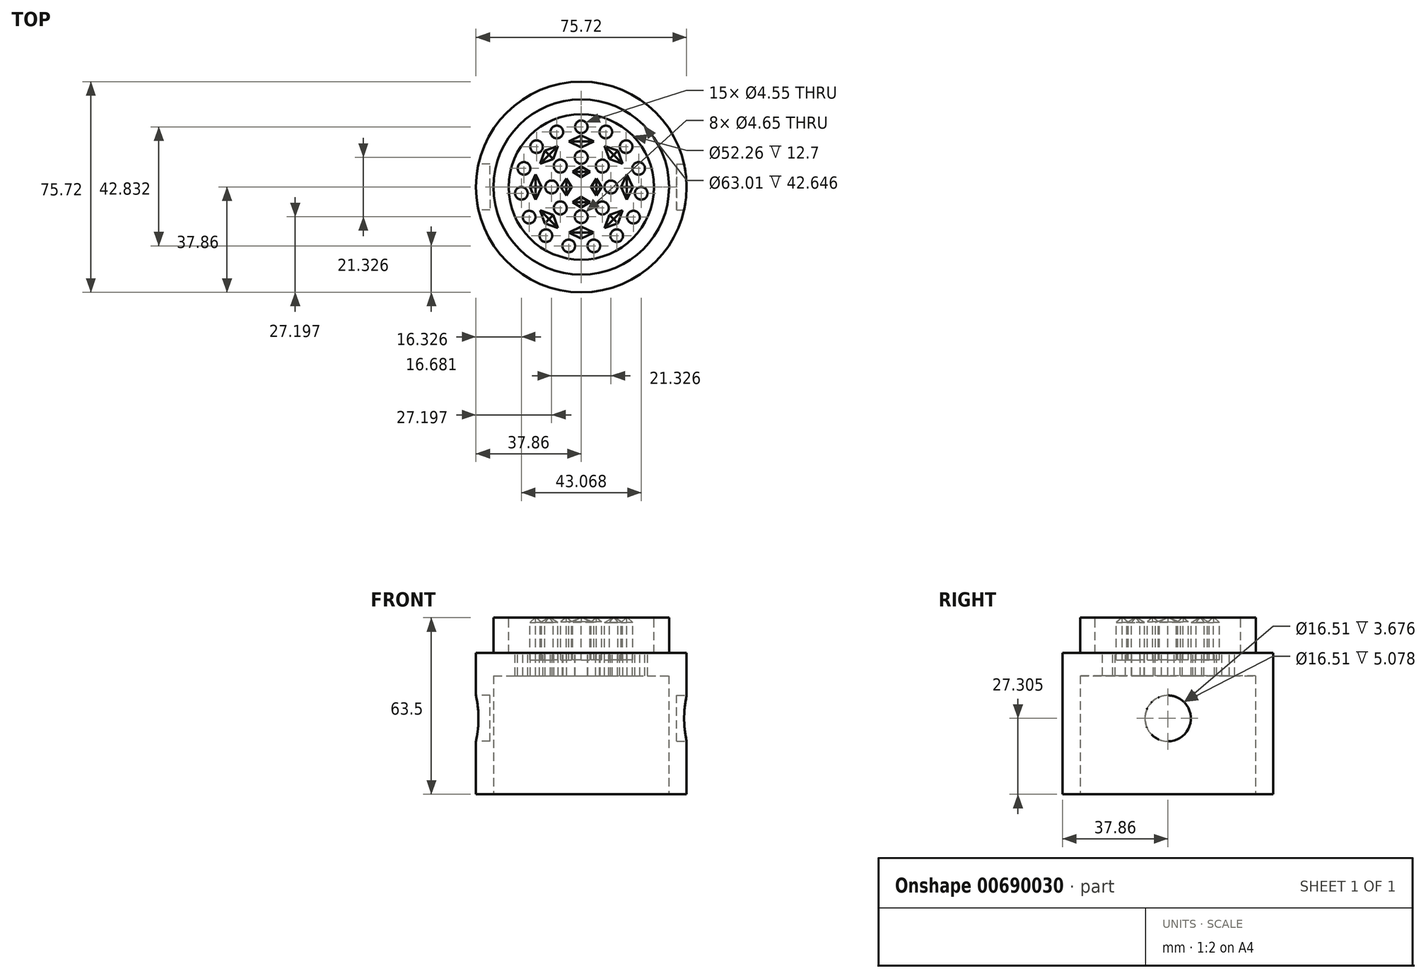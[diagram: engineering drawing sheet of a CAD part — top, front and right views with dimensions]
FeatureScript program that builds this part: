
annotation { "Feature Type Name" : "Feature", "Feature Type Description" : "" }
export const myFeature = defineFeature(function(context is Context, id is Id, definition is map)
    precondition{}
    {
        {
            var Q0;
            Q0=qCreatedBy(makeId("Top.planeOp"),FACE);
            var sketch = newSketch(context, id + "F0", { "sketchPlane" : qUnion([Q0])});
            skCircle(sketch, "E0", {"center": v(0, 0) * mm, "radius": 37.86 * mm});
            skCircle(sketch, "E1", {"center": v(0, 0) * mm, "radius": 31.55 * mm});
            skCircle(sketch, "E2", {"center": v(0, 0) * mm, "radius": 26.13 * mm});
            skCircle(sketch, "E3", {"center": v(0, 0) * mm, "radius": 18.32 * mm});
            skCircle(sketch, "E4", {"center": v(0, 0) * mm, "radius": 14.26 * mm});
            skCircle(sketch, "E5", {"center": v(0, 0) * mm, "radius": 7.5 * mm});
            skCircle(sketch, "E6", {"center": v(0, 0) * mm, "radius": 3.72 * mm});
            skSolve(sketch);
        }
        {
            var Q0;
            Q0=makeQuery(id+"F0.imprint","IMPRINT",FACE,{"disambiguationData":[TD([[makeQuery(id+"F0.imprint","IMPRINT",EDGE,{"derivedFrom":sQuery(id+"F0.wireOp",EDGE,"E0")}),1.0]])]});
            var Q1;
            Q1=makeQuery(id+"F0.imprint","IMPRINT",FACE,{"disambiguationData":[TD([[makeQuery(id+"F0.imprint","IMPRINT",EDGE,{"derivedFrom":sQuery(id+"F0.wireOp",EDGE,"E1")}),1.0]])]});
            var Q2;
            Q2=makeQuery(id+"F0.imprint","IMPRINT",FACE,{"disambiguationData":[TD([[makeQuery(id+"F0.imprint","IMPRINT",EDGE,{"derivedFrom":sQuery(id+"F0.wireOp",EDGE,"E3")}),1.0]])]});
            var Q3;
            Q3=makeQuery(id+"F0.imprint","IMPRINT",FACE,{"disambiguationData":[TD([[makeQuery(id+"F0.imprint","IMPRINT",EDGE,{"derivedFrom":sQuery(id+"F0.wireOp",EDGE,"E4")}),1.0]])]});
            var Q4;
            Q4=makeQuery(id+"F0.imprint","IMPRINT",FACE,{"disambiguationData":[TD([[makeQuery(id+"F0.imprint","IMPRINT",EDGE,{"derivedFrom":sQuery(id+"F0.wireOp",EDGE,"E2")}),1.0]])]});
            var Q5;
            Q5=makeQuery(id+"F0.imprint","IMPRINT",FACE,{"disambiguationData":[TD([[makeQuery(id+"F0.imprint","IMPRINT",EDGE,{"derivedFrom":sQuery(id+"F0.wireOp",EDGE,"E5")}),1.0]])]});
            var Q6;
            Q6=makeQuery(id+"F0.imprint","IMPRINT",FACE,{"disambiguationData":[TD([[makeQuery(id+"F0.imprint","IMPRINT",EDGE,{"derivedFrom":sQuery(id+"F0.wireOp",EDGE,"E6")}),1.0]])]});
            extrude(context, id + "F1", {"entities" : qUnion([Q0, Q1, Q2, Q3, Q4, Q5, Q6]), "oppositeDirection" : true, "depth" : 63.5 * mm, "offsetDistance" : 25.4 * mm});
        }
        {
            var Q0;
            Q0=makeQuery(id+"F0.imprint","IMPRINT",FACE,{"disambiguationData":[TD([[makeQuery(id+"F0.imprint","IMPRINT",EDGE,{"derivedFrom":sQuery(id+"F0.wireOp",EDGE,"E0")}),1.0]])]});
            var Q1;
            Q1=makeQuery(id+"F0.imprint","IMPRINT",FACE,{"disambiguationData":[TD([[makeQuery(id+"F0.imprint","IMPRINT",EDGE,{"derivedFrom":sQuery(id+"F0.wireOp",EDGE,"E2")}),1.0]])]});
            var Q2;
            Q2=makeQuery(id+"F0.imprint","IMPRINT",FACE,{"disambiguationData":[TD([[makeQuery(id+"F0.imprint","IMPRINT",EDGE,{"derivedFrom":sQuery(id+"F0.wireOp",EDGE,"E4")}),1.0]])]});
            var Q3;
            Q3=makeQuery(id+"F0.imprint","IMPRINT",FACE,{"disambiguationData":[TD([[makeQuery(id+"F0.imprint","IMPRINT",EDGE,{"derivedFrom":sQuery(id+"F0.wireOp",EDGE,"E6")}),1.0]])]});
            extrude(context, id + "F2", {"entities" : qUnion([Q0, Q1, Q2, Q3]), "operationType" : NewBodyOperationType.REMOVE, "oppositeDirection" : true, "depth" : 12.7 * mm, "offsetDistance" : 25.4 * mm});
        }
        {
            var Q0;
            Q0=qCreatedBy(makeId("Top.planeOp"),FACE);
            var sketch = newSketch(context, id + "F3", { "sketchPlane" : qUnion([Q0])});
            skLineSegment(sketch, "E7", {"start": v(0, 3.51) * mm, "end": v(0, 7.35) * mm});
            skLineSegment(sketch, "E8", {"start": v(0, 7.35) * mm, "end": v(-3.07, 5.43) * mm});
            skPoint(sketch, "E8.endSnap0", {"position": v(0, 5.43) * mm});
            skLineSegment(sketch, "E9", {"start": v(-3.07, 5.43) * mm, "end": v(0, 3.51) * mm});
            skLineSegment(sketch, "E10.MirrorCS", {"start": v(0, 7.35) * mm, "end": v(3.07, 5.43) * mm});
            skLineSegment(sketch, "E11.MirrorCS", {"start": v(3.07, 5.43) * mm, "end": v(0, 3.51) * mm});
            skLineSegment(sketch, "E12.1.0", {"start": v(-7.35, 0) * mm, "end": v(-5.43, -3.07) * mm});
            skLineSegment(sketch, "E12.1.1", {"start": v(-5.43, -3.07) * mm, "end": v(-3.51, 0) * mm});
            skLineSegment(sketch, "E12.1.2", {"start": v(-5.43, 3.07) * mm, "end": v(-3.51, 0) * mm});
            skLineSegment(sketch, "E12.1.3", {"start": v(-7.35, 0) * mm, "end": v(-5.43, 3.07) * mm});
            skLineSegment(sketch, "E12.2.0", {"start": v(0, -7.35) * mm, "end": v(3.07, -5.43) * mm});
            skLineSegment(sketch, "E12.2.1", {"start": v(3.07, -5.43) * mm, "end": v(0, -3.51) * mm});
            skLineSegment(sketch, "E12.2.2", {"start": v(-3.07, -5.43) * mm, "end": v(0, -3.51) * mm});
            skLineSegment(sketch, "E12.2.3", {"start": v(0, -7.35) * mm, "end": v(-3.07, -5.43) * mm});
            skLineSegment(sketch, "E12.3.0", {"start": v(7.35, 0) * mm, "end": v(5.43, 3.07) * mm});
            skLineSegment(sketch, "E12.3.1", {"start": v(5.43, 3.07) * mm, "end": v(3.51, 0) * mm});
            skLineSegment(sketch, "E12.3.2", {"start": v(5.43, -3.07) * mm, "end": v(3.51, 0) * mm});
            skLineSegment(sketch, "E12.3.3", {"start": v(7.35, 0) * mm, "end": v(5.43, -3.07) * mm});
            skPoint(sketch, "E12.center", {"position": v(0, 0) * mm});
            skLineSegment(sketch, "E13", {"start": v(0, 14.27) * mm, "end": v(0, 18.53) * mm});
            skLineSegment(sketch, "E14", {"start": v(0, 18.53) * mm, "end": v(-4.52, 16.4) * mm});
            skPoint(sketch, "E14.endSnap0", {"position": v(0, 16.4) * mm});
            skLineSegment(sketch, "E15", {"start": v(-4.52, 16.4) * mm, "end": v(0, 14.27) * mm});
            skLineSegment(sketch, "E16.MirrorCS", {"start": v(4.52, 16.4) * mm, "end": v(0, 14.27) * mm});
            skLineSegment(sketch, "E17.MirrorCS", {"start": v(0, 18.53) * mm, "end": v(4.52, 16.4) * mm});
            skLineSegment(sketch, "E18.1.0", {"start": v(-13.1, 13.1) * mm, "end": v(-14.8, 8.4) * mm});
            skLineSegment(sketch, "E18.1.1", {"start": v(-14.8, 8.4) * mm, "end": v(-10.1, 10.1) * mm});
            skLineSegment(sketch, "E18.1.2", {"start": v(-8.4, 14.8) * mm, "end": v(-10.1, 10.1) * mm});
            skLineSegment(sketch, "E18.1.3", {"start": v(-13.1, 13.1) * mm, "end": v(-8.4, 14.8) * mm});
            skLineSegment(sketch, "E18.2.0", {"start": v(-18.53, 0) * mm, "end": v(-16.4, -4.52) * mm});
            skLineSegment(sketch, "E18.2.1", {"start": v(-16.4, -4.52) * mm, "end": v(-14.27, 0) * mm});
            skLineSegment(sketch, "E18.2.2", {"start": v(-16.4, 4.52) * mm, "end": v(-14.27, 0) * mm});
            skLineSegment(sketch, "E18.2.3", {"start": v(-18.53, 0) * mm, "end": v(-16.4, 4.52) * mm});
            skLineSegment(sketch, "E18.3.0", {"start": v(-13.1, -13.1) * mm, "end": v(-8.4, -14.8) * mm});
            skLineSegment(sketch, "E18.3.1", {"start": v(-8.4, -14.8) * mm, "end": v(-10.1, -10.1) * mm});
            skLineSegment(sketch, "E18.3.2", {"start": v(-14.8, -8.4) * mm, "end": v(-10.1, -10.1) * mm});
            skLineSegment(sketch, "E18.3.3", {"start": v(-13.1, -13.1) * mm, "end": v(-14.8, -8.4) * mm});
            skLineSegment(sketch, "E18.4.0", {"start": v(0, -18.53) * mm, "end": v(4.52, -16.4) * mm});
            skLineSegment(sketch, "E18.4.1", {"start": v(4.52, -16.4) * mm, "end": v(0, -14.27) * mm});
            skLineSegment(sketch, "E18.4.2", {"start": v(-4.52, -16.4) * mm, "end": v(0, -14.27) * mm});
            skLineSegment(sketch, "E18.4.3", {"start": v(0, -18.53) * mm, "end": v(-4.52, -16.4) * mm});
            skLineSegment(sketch, "E18.5.0", {"start": v(13.1, -13.1) * mm, "end": v(14.8, -8.4) * mm});
            skLineSegment(sketch, "E18.5.1", {"start": v(14.8, -8.4) * mm, "end": v(10.1, -10.1) * mm});
            skLineSegment(sketch, "E18.5.2", {"start": v(8.4, -14.8) * mm, "end": v(10.1, -10.1) * mm});
            skLineSegment(sketch, "E18.5.3", {"start": v(13.1, -13.1) * mm, "end": v(8.4, -14.8) * mm});
            skLineSegment(sketch, "E18.6.0", {"start": v(18.53, 0) * mm, "end": v(16.4, 4.52) * mm});
            skLineSegment(sketch, "E18.6.1", {"start": v(16.4, 4.52) * mm, "end": v(14.27, 0) * mm});
            skLineSegment(sketch, "E18.6.2", {"start": v(16.4, -4.52) * mm, "end": v(14.27, 0) * mm});
            skLineSegment(sketch, "E18.6.3", {"start": v(18.53, 0) * mm, "end": v(16.4, -4.52) * mm});
            skLineSegment(sketch, "E18.7.0", {"start": v(13.1, 13.1) * mm, "end": v(8.4, 14.8) * mm});
            skLineSegment(sketch, "E18.7.1", {"start": v(8.4, 14.8) * mm, "end": v(10.1, 10.1) * mm});
            skLineSegment(sketch, "E18.7.2", {"start": v(14.8, 8.4) * mm, "end": v(10.1, 10.1) * mm});
            skLineSegment(sketch, "E18.7.3", {"start": v(13.1, 13.1) * mm, "end": v(14.8, 8.4) * mm});
            skSolve(sketch);
        }
        {
            var Q0;
            Q0=qCreatedBy(makeId("Top.planeOp"),FACE);
            var sketch = newSketch(context, id + "F4", { "sketchPlane" : qUnion([Q0])});
            skCircle(sketch, "E19", {"center": v(0, 0) * mm, "radius": 23.1 * mm});
            skSolve(sketch);
        }
        {
            var Q0;
            Q0 = qSketchRegion(id + "F4", true);
            extrude(context, id + "F5", {"entities" : qUnion([Q0]), "operationType" : NewBodyOperationType.REMOVE, "oppositeDirection" : true, "depth" : 12.7 * mm, "offsetDistance" : 25.4 * mm});
        }
        {
            var Q0;
            Q0 = qSketchRegion(id + "F3", true);
            extrude(context, id + "F6", {"entities" : qUnion([Q0]), "oppositeDirection" : true, "depth" : 15.24 * mm, "offsetDistance" : 25.4 * mm});
        }
        {
            var Q0;
            Q0=makeQuery(id+"F6.opExtrude","CAP_EDGE",EDGE,{"disambiguationData":[OSD([sQuery(id+"F3.wireOp",EDGE,"E18.2.0")])],"isStart":true});
            var Q1;
            Q1=makeQuery(id+"F6.opExtrude","CAP_EDGE",EDGE,{"disambiguationData":[OSD([sQuery(id+"F3.wireOp",EDGE,"E18.2.3")])],"isStart":true});
            var Q2;
            Q2=makeQuery(id+"F6.opExtrude","CAP_EDGE",EDGE,{"disambiguationData":[OSD([sQuery(id+"F3.wireOp",EDGE,"E18.2.2")])],"isStart":true});
            var Q3;
            Q3=makeQuery(id+"F6.opExtrude","CAP_EDGE",EDGE,{"disambiguationData":[OSD([sQuery(id+"F3.wireOp",EDGE,"E18.2.1")])],"isStart":true});
            var Q4;
            Q4=makeQuery(id+"F6.opExtrude","CAP_EDGE",EDGE,{"disambiguationData":[OSD([sQuery(id+"F3.wireOp",EDGE,"E18.3.3")])],"isStart":true});
            var Q5;
            Q5=makeQuery(id+"F6.opExtrude","CAP_EDGE",EDGE,{"disambiguationData":[OSD([sQuery(id+"F3.wireOp",EDGE,"E18.3.1")])],"isStart":true});
            var Q6;
            Q6=makeQuery(id+"F6.opExtrude","CAP_EDGE",EDGE,{"disambiguationData":[OSD([sQuery(id+"F3.wireOp",EDGE,"E18.3.2")])],"isStart":true});
            var Q7;
            Q7=makeQuery(id+"F6.opExtrude","CAP_EDGE",EDGE,{"disambiguationData":[OSD([sQuery(id+"F3.wireOp",EDGE,"E18.3.0")])],"isStart":true});
            var Q8;
            Q8=makeQuery(id+"F6.opExtrude","CAP_EDGE",EDGE,{"disambiguationData":[OSD([sQuery(id+"F3.wireOp",EDGE,"E18.4.2")])],"isStart":true});
            var Q9;
            Q9=makeQuery(id+"F6.opExtrude","CAP_EDGE",EDGE,{"disambiguationData":[OSD([sQuery(id+"F3.wireOp",EDGE,"E18.4.3")])],"isStart":true});
            var Q10;
            Q10=makeQuery(id+"F6.opExtrude","CAP_EDGE",EDGE,{"disambiguationData":[OSD([sQuery(id+"F3.wireOp",EDGE,"E18.4.1")])],"isStart":true});
            var Q11;
            Q11=makeQuery(id+"F6.opExtrude","CAP_EDGE",EDGE,{"disambiguationData":[OSD([sQuery(id+"F3.wireOp",EDGE,"E18.4.0")])],"isStart":true});
            var Q12;
            Q12=makeQuery(id+"F6.opExtrude","CAP_EDGE",EDGE,{"disambiguationData":[OSD([sQuery(id+"F3.wireOp",EDGE,"E18.5.3")])],"isStart":true});
            var Q13;
            Q13=makeQuery(id+"F6.opExtrude","CAP_EDGE",EDGE,{"disambiguationData":[OSD([sQuery(id+"F3.wireOp",EDGE,"E18.5.2")])],"isStart":true});
            var Q14;
            Q14=makeQuery(id+"F6.opExtrude","CAP_EDGE",EDGE,{"disambiguationData":[OSD([sQuery(id+"F3.wireOp",EDGE,"E18.5.1")])],"isStart":true});
            var Q15;
            Q15=makeQuery(id+"F6.opExtrude","CAP_EDGE",EDGE,{"disambiguationData":[OSD([sQuery(id+"F3.wireOp",EDGE,"E18.5.0")])],"isStart":true});
            var Q16;
            Q16=makeQuery(id+"F6.opExtrude","CAP_EDGE",EDGE,{"disambiguationData":[OSD([sQuery(id+"F3.wireOp",EDGE,"E18.1.1")])],"isStart":true});
            var Q17;
            Q17=makeQuery(id+"F6.opExtrude","CAP_EDGE",EDGE,{"disambiguationData":[OSD([sQuery(id+"F3.wireOp",EDGE,"E18.1.2")])],"isStart":true});
            var Q18;
            Q18=makeQuery(id+"F6.opExtrude","CAP_EDGE",EDGE,{"disambiguationData":[OSD([sQuery(id+"F3.wireOp",EDGE,"E18.1.3")])],"isStart":true});
            var Q19;
            Q19=makeQuery(id+"F6.opExtrude","CAP_EDGE",EDGE,{"disambiguationData":[OSD([sQuery(id+"F3.wireOp",EDGE,"E18.1.0")])],"isStart":true});
            var Q20;
            Q20=makeQuery(id+"F6.opExtrude","CAP_EDGE",EDGE,{"disambiguationData":[OSD([sQuery(id+"F3.wireOp",EDGE,"E18.6.1")])],"isStart":true});
            var Q21;
            Q21=makeQuery(id+"F6.opExtrude","CAP_EDGE",EDGE,{"disambiguationData":[OSD([sQuery(id+"F3.wireOp",EDGE,"E18.6.2")])],"isStart":true});
            var Q22;
            Q22=makeQuery(id+"F6.opExtrude","CAP_EDGE",EDGE,{"disambiguationData":[OSD([sQuery(id+"F3.wireOp",EDGE,"E18.6.3")])],"isStart":true});
            var Q23;
            Q23=makeQuery(id+"F6.opExtrude","CAP_EDGE",EDGE,{"disambiguationData":[OSD([sQuery(id+"F3.wireOp",EDGE,"E18.6.0")])],"isStart":true});
            var Q24;
            Q24=makeQuery(id+"F6.opExtrude","CAP_EDGE",EDGE,{"disambiguationData":[OSD([sQuery(id+"F3.wireOp",EDGE,"E18.7.3")])],"isStart":true});
            var Q25;
            Q25=makeQuery(id+"F6.opExtrude","CAP_EDGE",EDGE,{"disambiguationData":[OSD([sQuery(id+"F3.wireOp",EDGE,"E18.7.0")])],"isStart":true});
            var Q26;
            Q26=makeQuery(id+"F6.opExtrude","CAP_EDGE",EDGE,{"disambiguationData":[OSD([sQuery(id+"F3.wireOp",EDGE,"E18.7.1")])],"isStart":true});
            var Q27;
            Q27=makeQuery(id+"F6.opExtrude","CAP_EDGE",EDGE,{"disambiguationData":[OSD([sQuery(id+"F3.wireOp",EDGE,"E18.7.2")])],"isStart":true});
            var Q28;
            Q28=makeQuery(id+"F6.opExtrude","CAP_EDGE",EDGE,{"disambiguationData":[OSD([sQuery(id+"F3.wireOp",EDGE,"E16.MirrorCS")])],"isStart":true});
            var Q29;
            Q29=makeQuery(id+"F6.opExtrude","CAP_EDGE",EDGE,{"disambiguationData":[OSD([sQuery(id+"F3.wireOp",EDGE,"E15")])],"isStart":true});
            var Q30;
            Q30=makeQuery(id+"F6.opExtrude","CAP_EDGE",EDGE,{"disambiguationData":[OSD([sQuery(id+"F3.wireOp",EDGE,"E14")])],"isStart":true});
            var Q31;
            Q31=makeQuery(id+"F6.opExtrude","CAP_EDGE",EDGE,{"disambiguationData":[OSD([sQuery(id+"F3.wireOp",EDGE,"E17.MirrorCS")])],"isStart":true});
            chamfer(context, id + "F7", {"entities" : qUnion([Q0, Q1, Q2, Q3, Q4, Q5, Q6, Q7, Q8, Q9, Q10, Q11, Q12, Q13, Q14, Q15, Q16, Q17, Q18, Q19, Q20, Q21, Q22, Q23, Q24, Q25, Q26, Q27, Q28, Q29, Q30, Q31]), "width" : 1.78 * mm, "tangentPropagation" : true});
        }
        {
            var Q0;
            Q0=makeQuery(id+"F6.opExtrude","CAP_EDGE",EDGE,{"disambiguationData":[OSD([sQuery(id+"F3.wireOp",EDGE,"E8")])],"isStart":true});
            var Q1;
            Q1=makeQuery(id+"F6.opExtrude","CAP_EDGE",EDGE,{"disambiguationData":[OSD([sQuery(id+"F3.wireOp",EDGE,"E9")])],"isStart":true});
            var Q2;
            Q2=makeQuery(id+"F6.opExtrude","CAP_EDGE",EDGE,{"disambiguationData":[OSD([sQuery(id+"F3.wireOp",EDGE,"E11.MirrorCS")])],"isStart":true});
            var Q3;
            Q3=makeQuery(id+"F6.opExtrude","CAP_EDGE",EDGE,{"disambiguationData":[OSD([sQuery(id+"F3.wireOp",EDGE,"E10.MirrorCS")])],"isStart":true});
            var Q4;
            Q4=makeQuery(id+"F6.opExtrude","CAP_EDGE",EDGE,{"disambiguationData":[OSD([sQuery(id+"F3.wireOp",EDGE,"E12.3.1")])],"isStart":true});
            var Q5;
            Q5=makeQuery(id+"F6.opExtrude","CAP_EDGE",EDGE,{"disambiguationData":[OSD([sQuery(id+"F3.wireOp",EDGE,"E12.3.0")])],"isStart":true});
            var Q6;
            Q6=makeQuery(id+"F6.opExtrude","CAP_EDGE",EDGE,{"disambiguationData":[OSD([sQuery(id+"F3.wireOp",EDGE,"E12.3.3")])],"isStart":true});
            var Q7;
            Q7=makeQuery(id+"F6.opExtrude","CAP_EDGE",EDGE,{"disambiguationData":[OSD([sQuery(id+"F3.wireOp",EDGE,"E12.3.2")])],"isStart":true});
            var Q8;
            Q8=makeQuery(id+"F6.opExtrude","CAP_EDGE",EDGE,{"disambiguationData":[OSD([sQuery(id+"F3.wireOp",EDGE,"E12.2.0")])],"isStart":true});
            var Q9;
            Q9=makeQuery(id+"F6.opExtrude","CAP_EDGE",EDGE,{"disambiguationData":[OSD([sQuery(id+"F3.wireOp",EDGE,"E12.2.1")])],"isStart":true});
            var Q10;
            Q10=makeQuery(id+"F6.opExtrude","CAP_EDGE",EDGE,{"disambiguationData":[OSD([sQuery(id+"F3.wireOp",EDGE,"E12.2.2")])],"isStart":true});
            var Q11;
            Q11=makeQuery(id+"F6.opExtrude","CAP_EDGE",EDGE,{"disambiguationData":[OSD([sQuery(id+"F3.wireOp",EDGE,"E12.2.3")])],"isStart":true});
            var Q12;
            Q12=makeQuery(id+"F6.opExtrude","CAP_EDGE",EDGE,{"disambiguationData":[OSD([sQuery(id+"F3.wireOp",EDGE,"E12.1.1")])],"isStart":true});
            var Q13;
            Q13=makeQuery(id+"F6.opExtrude","CAP_EDGE",EDGE,{"disambiguationData":[OSD([sQuery(id+"F3.wireOp",EDGE,"E12.1.0")])],"isStart":true});
            var Q14;
            Q14=makeQuery(id+"F6.opExtrude","CAP_EDGE",EDGE,{"disambiguationData":[OSD([sQuery(id+"F3.wireOp",EDGE,"E12.1.3")])],"isStart":true});
            var Q15;
            Q15=makeQuery(id+"F6.opExtrude","CAP_EDGE",EDGE,{"disambiguationData":[OSD([sQuery(id+"F3.wireOp",EDGE,"E12.1.2")])],"isStart":true});
            chamfer(context, id + "F8", {"entities" : qUnion([Q0, Q1, Q2, Q3, Q4, Q5, Q6, Q7, Q8, Q9, Q10, Q11, Q12, Q13, Q14, Q15]), "width" : 1.52 * mm, "tangentPropagation" : true});
        }
        {
            var Q0;
            Q0=makeQuery(id+"F1.opExtrude","CAP_FACE",FACE,{"disambiguationData":[OSD([sQuery(id+"F0.wireOp",EDGE,"E0")])],"isStart":false});
            var sketch = newSketch(context, id + "F9", { "sketchPlane" : qUnion([Q0])});
            skCircle(sketch, "E20", {"center": v(0, 0) * mm, "radius": 31.5 * mm});
            skSolve(sketch);
        }
        {
            var Q0;
            Q0=makeQuery(id+"F9.imprint","IMPRINT",FACE,{"disambiguationData":[TD([[makeQuery(id+"F9.imprint","IMPRINT",EDGE,{"derivedFrom":sQuery(id+"F9.wireOp",EDGE,"E20")}),1.0]])]});
            extrude(context, id + "F10", {"entities" : qUnion([Q0]), "operationType" : NewBodyOperationType.REMOVE, "oppositeDirection" : true, "depth" : 42.65 * mm, "offsetDistance" : 25.4 * mm});
        }
        {
            var Q0;
            Q0=makeQuery(id+"F5.boolean.opBoolean","MERGE",FACE,{"derivedFrom":[makeQuery(id+"F2.boolean.opBoolean","COPY",FACE,{"derivedFrom":makeQuery(id+"F2.opExtrude","CAP_FACE",FACE,{"disambiguationData":[OSD([sQuery(id+"F0.wireOp",EDGE,"E2"),sQuery(id+"F0.wireOp",EDGE,"E3")])],"isStart":false})}),makeQuery(id+"F2.boolean.opBoolean","COPY",FACE,{"derivedFrom":makeQuery(id+"F2.opExtrude","CAP_FACE",FACE,{"disambiguationData":[OSD([sQuery(id+"F0.wireOp",EDGE,"E4"),sQuery(id+"F0.wireOp",EDGE,"E5")])],"isStart":false})}),makeQuery(id+"F2.boolean.opBoolean","COPY",FACE,{"derivedFrom":makeQuery(id+"F2.opExtrude","CAP_FACE",FACE,{"disambiguationData":[OSD([sQuery(id+"F0.wireOp",EDGE,"E6")])],"isStart":false})}),makeQuery(id+"F5.opExtrude","CAP_FACE",FACE,{"disambiguationData":[OSD([sQuery(id+"F4.wireOp",EDGE,"E19")])],"isStart":false})]});
            var sketch = newSketch(context, id + "F11", { "sketchPlane" : qUnion([Q0])});
            skCircle(sketch, "E21", {"center": v(0, 21.65) * mm, "radius": 2.27 * mm});
            skCircle(sketch, "E22.1.0", {"center": v(-8.8, 19.78) * mm, "radius": 2.27 * mm});
            skCircle(sketch, "E22.2.0", {"center": v(-16.1, 14.49) * mm, "radius": 2.27 * mm});
            skCircle(sketch, "E22.3.0", {"center": v(-20.6, 6.7) * mm, "radius": 2.27 * mm});
            skCircle(sketch, "E22.4.0", {"center": v(-21.53, -2.26) * mm, "radius": 2.27 * mm});
            skCircle(sketch, "E22.5.0", {"center": v(-18.75, -10.83) * mm, "radius": 2.27 * mm});
            skCircle(sketch, "E22.6.0", {"center": v(-12.73, -17.52) * mm, "radius": 2.27 * mm});
            skCircle(sketch, "E22.7.0", {"center": v(-4.5, -21.18) * mm, "radius": 2.27 * mm});
            skCircle(sketch, "E22.8.0", {"center": v(4.5, -21.18) * mm, "radius": 2.27 * mm});
            skCircle(sketch, "E22.9.0", {"center": v(12.73, -17.52) * mm, "radius": 2.27 * mm});
            skCircle(sketch, "E22.10.0", {"center": v(18.75, -10.83) * mm, "radius": 2.27 * mm});
            skCircle(sketch, "E22.11.0", {"center": v(21.53, -2.26) * mm, "radius": 2.27 * mm});
            skCircle(sketch, "E22.12.0", {"center": v(20.6, 6.7) * mm, "radius": 2.27 * mm});
            skCircle(sketch, "E22.13.0", {"center": v(16.1, 14.49) * mm, "radius": 2.27 * mm});
            skCircle(sketch, "E22.14.0", {"center": v(8.8, 19.78) * mm, "radius": 2.27 * mm});
            skPoint(sketch, "E22.center", {"position": v(0, 0) * mm});
            skCircle(sketch, "E23", {"center": v(0, 10.66) * mm, "radius": 2.32 * mm});
            skCircle(sketch, "E24.1.0", {"center": v(-7.54, 7.54) * mm, "radius": 2.32 * mm});
            skCircle(sketch, "E24.2.0", {"center": v(-10.66, 0) * mm, "radius": 2.32 * mm});
            skCircle(sketch, "E24.3.0", {"center": v(-7.54, -7.54) * mm, "radius": 2.32 * mm});
            skCircle(sketch, "E24.4.0", {"center": v(0, -10.66) * mm, "radius": 2.32 * mm});
            skCircle(sketch, "E24.5.0", {"center": v(7.54, -7.54) * mm, "radius": 2.32 * mm});
            skCircle(sketch, "E24.6.0", {"center": v(10.66, 0) * mm, "radius": 2.32 * mm});
            skCircle(sketch, "E24.7.0", {"center": v(7.54, 7.54) * mm, "radius": 2.32 * mm});
            skSolve(sketch);
        }
        {
            var Q0;
            Q0 = qSketchRegion(id + "F11", true);
            extrude(context, id + "F12", {"entities" : qUnion([Q0]), "operationType" : NewBodyOperationType.REMOVE, "oppositeDirection" : true, "depth" : 25.4 * mm, "offsetDistance" : 25.4 * mm});
        }
        {
            var Q0;
            Q0=qCreatedBy(makeId("Right.planeOp"),FACE);
            cPlane(context, id + "F13", {"entities" : qUnion([Q0]), "cplaneType" : CPlaneType.OFFSET, "offset" : 53.66 * mm, "width" : 152.4 * mm, "height" : 152.4 * mm});
        }
        {
            var Q0;
            Q0=qCreatedBy(id+"F13.planeOp",FACE);
            var sketch = newSketch(context, id + "F14", { "sketchPlane" : qUnion([Q0])});
            skCircle(sketch, "E25", {"center": v(0, -36.2) * mm, "radius": 8.26 * mm});
            skSolve(sketch);
        }
        {
            var Q0;
            Q0=makeQuery(id+"F14.imprint","IMPRINT",FACE,{"disambiguationData":[TD([[makeQuery(id+"F14.imprint","IMPRINT",EDGE,{"derivedFrom":sQuery(id+"F14.wireOp",EDGE,"E25")}),1.0]])]});
            extrude(context, id + "F15", {"entities" : qUnion([Q0]), "operationType" : NewBodyOperationType.REMOVE, "oppositeDirection" : true, "depth" : 19.48 * mm, "offsetDistance" : 25.4 * mm});
        }
        {
            var Q0;
            Q0=qCreatedBy(makeId("Right.planeOp"),FACE);
            cPlane(context, id + "F16", {"entities" : qUnion([Q0]), "cplaneType" : CPlaneType.OFFSET, "offset" : 58.18 * mm, "oppositeDirection" : true, "width" : 152.4 * mm, "height" : 152.4 * mm});
        }
        {
            var Q0;
            Q0=qCreatedBy(id+"F16.planeOp",FACE);
            var sketch = newSketch(context, id + "F17", { "sketchPlane" : qUnion([Q0])});
            skCircle(sketch, "E26", {"center": v(0, -36.2) * mm, "radius": 8.26 * mm});
            skSolve(sketch);
        }
        {
            var Q0;
            Q0=makeQuery(id+"F17.imprint","IMPRINT",FACE,{"disambiguationData":[TD([[makeQuery(id+"F17.imprint","IMPRINT",EDGE,{"derivedFrom":sQuery(id+"F17.wireOp",EDGE,"E26")}),1.0]])]});
            extrude(context, id + "F18", {"entities" : qUnion([Q0]), "operationType" : NewBodyOperationType.REMOVE, "depth" : 25.4 * mm, "offsetDistance" : 25.4 * mm});
        }
    });
